# Revit family: QF_ELECTROLUXPROFESSIONAL_1LSP41_WH6-8CV_E
name_source: partatom
category: Attrezzature speciali
units: mm (PartAtom-declared; Revit-internal decimal feet)

## family parameters
Basato su piano di lavoro = No
Condiviso = No
Punto di calcolo locali = No
Quota connettore circolare = Usa diametro
Sempre verticale = Sì
Taglio con vuoti quando caricato = No
Tipo di parte = Normale

## types (40) — shared parameters
Latent Heat Output = 0.0
Length Actual = 720 mm  [stored 2.3622 ft]
Modello = WH6-8CV
Produttore = Electrolux Professional
Sensible Heat Output = 0.0
URL = www.electroluxprofessional.com
Weight = 158
zero-valued in all types: Gas KW, Prospetto di default, Steam Pounds per Hour

## per-type parameters (varying)
| type | Cycle | Depth Actual | Descrizione | Height Actual | Item Number | Phase | Volts | Watts |
| 9867630165 | 50 Hz | 720 mm  [stored 2.3622 ft] | WASHER WH6-8CV 8KG LE 3KW 380-415/50/3N CLARUS VIBE GEN+COIN 2xWATER POWDER TOP PREP.ID VALV.OPEN IS SILVER ELS-NETW. DI | 1130 mm  [stored 3.70735 ft] | 1L0GAA | 3 | 415 V | 3300 W |
| 9867630084 | 50 Hz | 720 mm  [stored 2.3622 ft] | WASHER WH6-8CV 8KG EL 7,5KW 440/50/3 CLARUS VIBE GEN+COIN 2xWATER POWDER TOP PREP.ID PUMP SILVER TRAFO 380-480 DISCON. | 1130 mm  [stored 3.70735 ft] | 1LSNUD | 3 | 440 V | 7800 W |
| 9867630031 | 50 Hz | 721 mm  [stored 2.36549 ft] | WASHER WH6-8CV 8KG EL 7,5KW 380-415/50/3N CLARUS VIBE GEN+COIN 2xWATER POWDER TOP PREP.ID VALV.OPEN SILVER ELS-NETW. DIS | 1132 mm  [stored 3.71391 ft] | 1L0HFF | 3 | 415 V | 7800 W |
| 9867630074 | 50 Hz | 720 mm  [stored 2.3622 ft] | WASHER WH6-8CV 8KG EL 7,5KW 380-400/50/3N CLARUS VIBE GEN+COIN 2xWATER POWDER TOP PREP.ID VALV.OPEN SST DISCON. | 1130 mm  [stored 3.70735 ft] | 1LSNPA | 3 | 415 V | 7800 W |
| 9867630265 | 50 Hz | 720 mm  [stored 2.3622 ft] | WASHER WH6-8CV 8KG EL 7,5KW 380-415/50/3N CLARUS VIBE GEN+COIN 2xWATER PREP.ID VALV.OPEN IS SILVER DISCON. | 1130 mm  [stored 3.70735 ft] | 1LSPJW | 3 | 415 V | 7800 W |
| 9867630019 | 50 Hz | 720 mm  [stored 2.3622 ft] | WASHER WH6-8CV 8KG LE 3KW 380-415/50/3N CLARUS VIBE GEN+COIN 2xWATER PREP.ID VALV.OPEN SILVER DISCON. | 1130 mm  [stored 3.70735 ft] | 1L0EWR | 3 | 415 V | 3300 W |
| 9867630029 | 50 Hz | 720 mm  [stored 2.3622 ft] | WASHER WH6-8CV 8KG LE 3KW 380-415/50/3N CLARUS VIBE GEN+COIN 2xWATER POWDER TOP PREP.ID VALV.OPEN IS SILVER DISCON. | 1130 mm  [stored 3.70735 ft] | 1LSNDY | 3 | 415 V | 3300 W |
| 9867630197 | 60 Hz | 720 mm  [stored 2.3622 ft] | WASHER WH6-8CV 8KG NO HEAT 208-240/60/1 CLARUS VIBE GEN+COIN 2xWATER POWDER TOP TRIGG.DOS. VALV.CLOSED IS SILVER X.I/O | 1130 mm  [stored 3.70735 ft] | 1LA1DN | 1 | 240 V | 1000 W |
| 9867630013 | 50 Hz | 720 mm  [stored 2.3622 ft] | WASHER WH6-8CV 8KG EL 7,5KW 380-415/50/3N CLARUS VIBE GEN+COIN 2xWATER PREP.ID VALV.OPEN SILVER ELS-NETW. DISCON. | 1130 mm  [stored 3.70735 ft] | 1L0EWK | 3 | 415 V | 7800 W |
| 9867630096 | 50 Hz | 720 mm  [stored 2.3622 ft] | WASHER WH6-8CV 8KG NO HEAT 220-240/50/1N CLARUS VIBE GEN+COIN 2xWATER PREP.ID VALV.OPEN SILVER EXT.PM. X.I/O DISCON. | 1130 mm  [stored 3.70735 ft] | 1L0G02 | 1 | 240 V | 1000 W |
| 9867630033 | 50 Hz | 720 mm  [stored 2.3622 ft] | WASHER WH6-8CV 8KG EL 7,5KW 380-415/50/3N CLARUS VIBE GEN+COIN 2xWATER POWDER TOP PREP.ID VALV.OPEN IS SILVER DISCON. | 1130 mm  [stored 3.70735 ft] | 1LSNJB | 3 | 415 V | 7800 W |
| 9867630066 | 50 Hz | 720 mm  [stored 2.3622 ft] | WASHER WH6-8CV 8KG EL 7,5KW 380-415/50/3N CLARUS VIBE GEN+COIN 2xWATER POWDER TOP TRIGG.DOS. VALV.OPEN SILVER X.I/O DISC | 1130 mm  [stored 3.70735 ft] | 1LSNP8 | 3 | 415 V | 7800 W |
| 9867630076 | 50 Hz | 720 mm  [stored 2.3622 ft] | WASHER WH6-8CV 8KG LE 3KW 380-415/50/3N CLARUS VIBE GEN+COIN 2xWATER PREP.ID VALV.OPEN IS SILVER DISCON. | 1130 mm  [stored 3.70735 ft] | 1LSNPW | 3 | 415 V | 3300 W |
| 9867630312 | 50 Hz | 721 mm  [stored 2.36549 ft] | WASHER WH6-8CV 8KG EL 7,5KW 380-415/50/3N CLARUS VIBE GEN+COIN 2xWATER POWDER TOP TRIGG.DOS. VALV.OPEN IS SILVER X.I/O D | 1132 mm  [stored 3.71391 ft] | 1LT665 | 3 | 415 V | 7800 W |
| 9867630154 | 50 Hz | 720 mm  [stored 2.3622 ft] | WASHER WH6-8CV 8KG MOP 7,5KW 380-400/50/3 CLARUS VIBE MOP 2xWATER POWDER TOP PREP.ID EL.VALV.OPEN SILVER TRAFO 380-480 D | 1130 mm  [stored 3.70735 ft] | 1L0G80 | 3 | 415 V | 7800 W |
| 9867630174 | 50 Hz | 720 mm  [stored 2.3622 ft] | WASHER WH6-8CV 8KG LE 3KW 380-415/50/3N CLARUS VIBE GEN+COIN 2xWATER POWDER TOP PREP.ID VALV.OPEN IS SILVER PREP.EXT.PM. | 1130 mm  [stored 3.70735 ft] | 1L0GCT | 3 | 415 V | 3300 W |
| 9867630104 | 50 Hz | 720 mm  [stored 2.3622 ft] | WASHER WH6-8CV 8KG EL 7,5KW 380-415/220-240/50/3N/1 CLARUS VIBE GEN+COIN 2xWATER POWDER TOP PREP.ID VALV.OPEN SILVER EXT | 1130 mm  [stored 3.70735 ft] | 1L0G0D | 3 | 415 V | 7800 W |
| 9867630085 | 50 Hz | 720 mm  [stored 2.3622 ft] | WASHER WH6-8CV 8KG EL 7,5KW 380-415/220-240/50/3N/3 CLARUS VIBE GEN+COIN 2xWATER POWDER TOP PREP.ID PUMP SILVER DISCON. | 1130 mm  [stored 3.70735 ft] | 1LSNWK | 3 | 415 V | 7800 W |
| 9867630025 | 50 Hz | 720 mm  [stored 2.3622 ft] | WASHER WH6-8CV 8KG EL 7,5KW 380-415/220-240/50/3N/1 CLARUS VIBE GEN+COIN 2xWATER POWDER TOP PREP.ID EL.VALV.OPEN SILVER | 1130 mm  [stored 3.70735 ft] | 1L0EWX | 3 | 415 V | 7800 W |
| 9867630035 | 50 Hz | 720 mm  [stored 2.3622 ft] | WASHER WH6-8CV 8KG MOP 7,5KW 220-230/50/3 CLARUS VIBE MOP 2xWATER POWDER TOP PREP.ID EL.VALV.OPEN SILVER DISCON. | 1130 mm  [stored 3.70735 ft] | 1LSNK6 | 3 | 240 V | 7800 W |
| 9867630151 | 50 Hz | 720 mm  [stored 2.3622 ft] | WASHER WH6-8CV 8KG LE 3KW 380-415/50/3N CLARUS VIBE GEN+COIN 2xWATER PREP.ID VALV.OPEN SILVER ELS-NETW. DISCON. | 1130 mm  [stored 3.70735 ft] | 1LSP7K | 3 | 415 V | 3300 W |
| 9867630310 | 50 Hz | 721 mm  [stored 2.36549 ft] | WASHER WH6-8CV 8KG MOP 7,5KW 380-415/50/3N CLARUS VIBE MOP 2xWATER POWDER TOP PREP.ID EL.VALV.OPEN IS SST DISCON. | 1132 mm  [stored 3.71391 ft] | 1LA260 | 3 | 415 V | 7800 W |
| 9867630080 | 50 Hz | 720 mm  [stored 2.3622 ft] | WASHER WH6-8CV 8KG MOP 7,5KW 380-415/50/3N CLARUS VIBE MOP 2xWATER POWDER TOP PREP.ID EL.VALV.CLOSED IS SILVER DISCON. | 1130 mm  [stored 3.70735 ft] | 1LSNTS | 3 | 415 V | 7800 W |
| 9867630291 | 50 Hz | 721 mm  [stored 2.36549 ft] | WASHER WH6-8CV 8KG EL 7,5KW 380-415/50/3 CLARUS VIBE GEN+COIN 2xWATER POWDER TOP PREP.ID VALV.OPEN IS SST TRAFO 380-480 | 1132 mm  [stored 3.71391 ft] | 1L0H54 | 3 | 415 V | 7800 W |
| 9867630090 | 50 Hz | 720 mm  [stored 2.3622 ft] | WASHER WH6-8CV 8KG NO HEAT 220-240/50/1N CLARUS VIBE GEN+COIN 2xWATER POWDER TOP PREP.ID VALV.OPEN SILVER EXT.PM. X.I/O | 1130 mm  [stored 3.70735 ft] | 1LSNXD | 1 | 240 V | 1000 W |
| 9867630020 | 50 Hz | 720 mm  [stored 2.3622 ft] | WASHER WH6-8CV 8KG MOP 7,5KW 380-400/50/3N CLARUS VIBE MOP 2xWATER POWDER TOP PREP.ID EL.VALV.CLOSED SILVER DISCON. | 1130 mm  [stored 3.70735 ft] | 1L0EWS | 3 | 415 V | 7800 W |
| 9867630087 | 50 Hz | 720 mm  [stored 2.3622 ft] | WASHER WH6-8CV 8KG EL 7,5KW 380-415/50/3N CLARUS VIBE GEN+COIN 2xWATER PREP.ID VALV.OPEN IS SILVER ELS-NETW. DISCON. | 1130 mm  [stored 3.70735 ft] | 1LSNWV | 3 | 415 V | 7800 W |
| 9867630264 | 60 Hz | 721 mm  [stored 2.36549 ft] | WASHER WH6-8CV 8KG EL 7,5KW 440/60/3 CLARUS VIBE GEN+COIN 2xWATER POWDER TOP TRIGG.DOS. EL.VALV.CLOSED IS SILVER X.I/O T | 1132 mm  [stored 3.71391 ft] | 1LSPHW | 3 | 440 V | 7800 W |
| 9867630067 | 50 Hz | 720 mm  [stored 2.3622 ft] | WASHER WH6-8CV 8KG EL 7,5KW 380-415/220-240/50/3N/1 CLARUS VIBE GEN+COIN 2xWATER POWDER TOP TRIGG.DOS. EL.VALV.OPEN SILV | 1130 mm  [stored 3.70735 ft] | 1LSNP9 | 3 | 415 V | 7800 W |
| 9867630078 | 50 Hz | 720 mm  [stored 2.3622 ft] | WASHER WH6-8CV 8KG EL 7,5KW 380-400/50/3N CLARUS VIBE GEN+COIN 2xWATER POWDER TOP PREP.ID VALV.OPEN SST/SILVER DISCON. | 1130 mm  [stored 3.70735 ft] | 1LSNPY | 3 | 415 V | 7800 W |
| 9867630007 | 50 Hz | 720 mm  [stored 2.3622 ft] | WASHER WH6-8CV 8KG EL 7,5KW 380-415/50/3N CLARUS VIBE GEN+COIN 2xWATER POWDER TOP PREP.ID VALV.OPEN SILVER DISCON. | 1130 mm  [stored 3.70735 ft] | 1L0EWE | 3 | 415 V | 7800 W |
| 9867630018 | 50 Hz | 720 mm  [stored 2.3622 ft] | WASHER WH6-8CV 8KG LE 3KW 380-415/50/3N CLARUS VIBE GEN+COIN 2xWATER POWDER TOP PREP.ID VALV.OPEN SILVER DISCON. | 1130 mm  [stored 3.70735 ft] | 1LSN99 | 3 | 415 V | 3300 W |
| 9867630027 | 50 Hz | 720 mm  [stored 2.3622 ft] | WASHER WH6-8CV 8KG EL 7,5KW 380-415/50/3N CLARUS VIBE GEN+COIN 2xWATER POWDER TOP PREP.ID VALV.OPEN IS SILVER ELS-NETW. | 1130 mm  [stored 3.70735 ft] | 1LSNE6 | 3 | 415 V | 7800 W |
| 9867630143 | 50 Hz | 720 mm  [stored 2.3622 ft] | WASHER WH6-8CV 8KG MOP 7,5KW 380-415/50/3N CLARUS VIBE MOP 2xWATER POWDER TOP PREP.ID EL.VALV.OPEN IS SILVER DISCON. | 1130 mm  [stored 3.70735 ft] | 1LA0A9 | 3 | 415 V | 3300 W |
| 9867630173 | 50 Hz | 720 mm  [stored 2.3622 ft] | WASHER WH6-8CV 8KG LE 3KW 380-415/50/3N CLARUS VIBE GEN+COIN 2xWATER PREP.ID VALV.OPEN IS SILVER ELS-NETW. DISCON. | 1130 mm  [stored 3.70735 ft] | 1L0GCS | 3 | 415 V | 3300 W |
| 9867630082 | 50 Hz | 720 mm  [stored 2.3622 ft] | WASHER WH6-8CV 8KG MOP 7,5KW 380-415/220-240/50/3N/3 CLARUS VIBE MOP 2xWATER POWDER TOP PREP.ID EL.VALV.OPEN SILVER DISC | 1130 mm  [stored 3.70735 ft] | 1LSNRX | 3 | 415 V | 7800 W |
| 9867630257 | 50 Hz | 720 mm  [stored 2.3622 ft] | WASHER WH6-8CV 8KG NO HEAT 200/50/60/3 CLARUS VIBE GEN+COIN 2xWATER PREP.ID VALV.OPEN SILVER DISCON. | 1130 mm  [stored 3.70735 ft] | 1LA250 | 3 | 200 V | 1000 W |
| 9867630012 | 50 Hz | 720 mm  [stored 2.3622 ft] | WASHER WH6-8CV 8KG MOP 7,5KW 380-400/50/3N CLARUS VIBE MOP 2xWATER POWDER TOP PREP.ID EL.VALV.OPEN SILVER DISCON. | 1130 mm  [stored 3.70735 ft] | 1L0EWJ | 3 | 415 V | 7800 W |
| 9867630032 | 50 Hz | 721 mm  [stored 2.36549 ft] | WASHER WH6-8CV 8KG EL 7,5KW 380-415/50/3N CLARUS VIBE GEN+COIN 2xWATER PREP.ID VALV.OPEN SILVER DISCON. | 1132 mm  [stored 3.71391 ft] | 1L0HFG | 3 | 415 V | 7800 W |
| 9867630150 | 50 Hz | 720 mm  [stored 2.3622 ft] | WASHER WH6-8CV 8KG NO HEAT 220-240/50/1N CLARUS VIBE GEN+COIN 2xWATER POWDER TOP PREP.ID VALV.OPEN IS SILVER PREP.EXT.PM | 1130 mm  [stored 3.70735 ft] | 1LSP6L | 1 | 240 V | 1000 W |

note: [stored X ft] marks values corroborated as IEEE doubles in the binary element streams (Revit-internal decimal feet)

## geometry (parser evidence)
native form markers: Blend x6
no freeform markers — native parametric forms only
